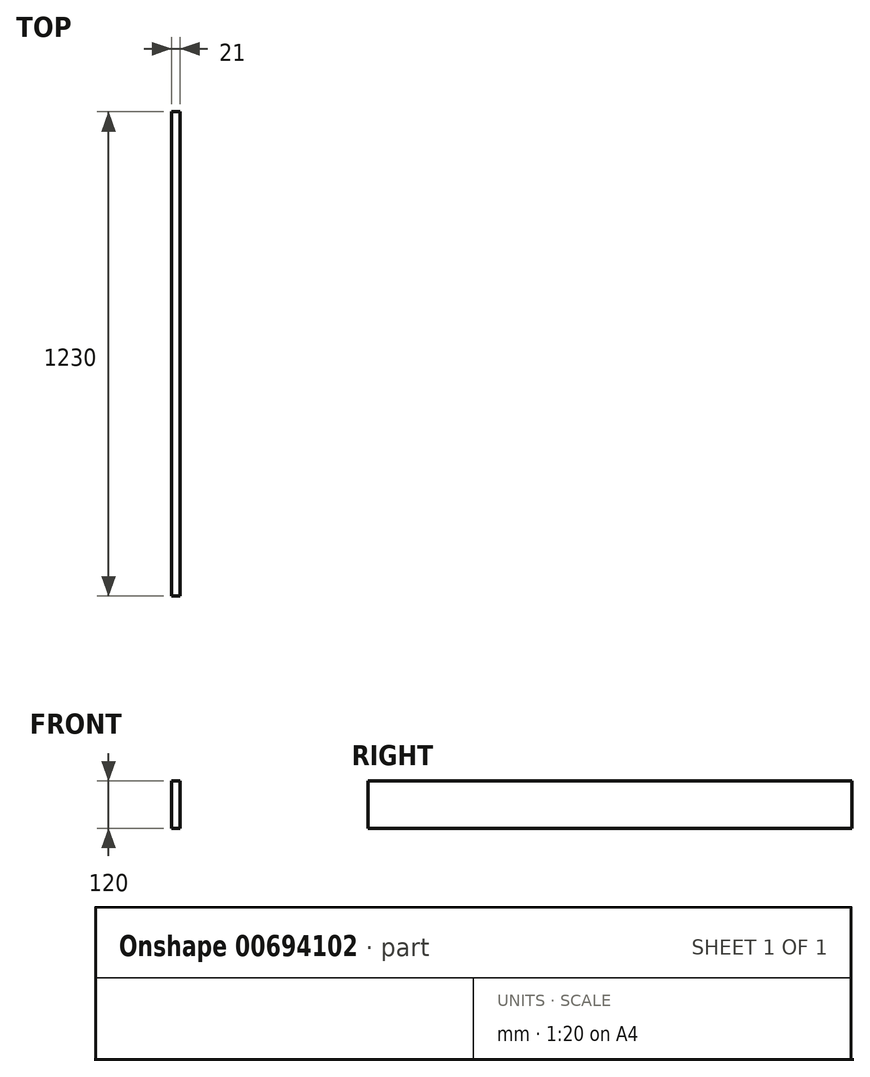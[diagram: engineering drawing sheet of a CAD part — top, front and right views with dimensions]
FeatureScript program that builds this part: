
annotation { "Feature Type Name" : "Feature", "Feature Type Description" : "" }
export const myFeature = defineFeature(function(context is Context, id is Id, definition is map)
    precondition{}
    {
        {
            var Q0;
            Q0=qCreatedBy(makeId("Right.planeOp"),FACE);
            var sketch = newSketch(context, id + "F0", { "sketchPlane" : qUnion([Q0])});
            skLineSegment(sketch, "E0.bottom", {"start": v(-615, -60) * mm, "end": v(615, -60) * mm});
            skLineSegment(sketch, "E0.top", {"start": v(-615, 60) * mm, "end": v(615, 60) * mm});
            skLineSegment(sketch, "E0.left", {"start": v(-615, -60) * mm, "end": v(-615, 60) * mm});
            skLineSegment(sketch, "E0.right", {"start": v(615, -60) * mm, "end": v(615, 60) * mm});
            skSolve(sketch);
        }
        {
            var Q0;
            Q0=makeQuery(id+"F0.imprint","IMPRINT",FACE,{"disambiguationData":[TD([[makeQuery(id+"F0.imprint","IMPRINT",EDGE,{"derivedFrom":sQuery(id+"F0.wireOp",EDGE,"E0.bottom")}),1.0]])]});
            extrude(context, id + "F1", {"entities" : qUnion([Q0]), "depth" : 21 * mm, "offsetDistance" : 25 * mm});
        }
    });
